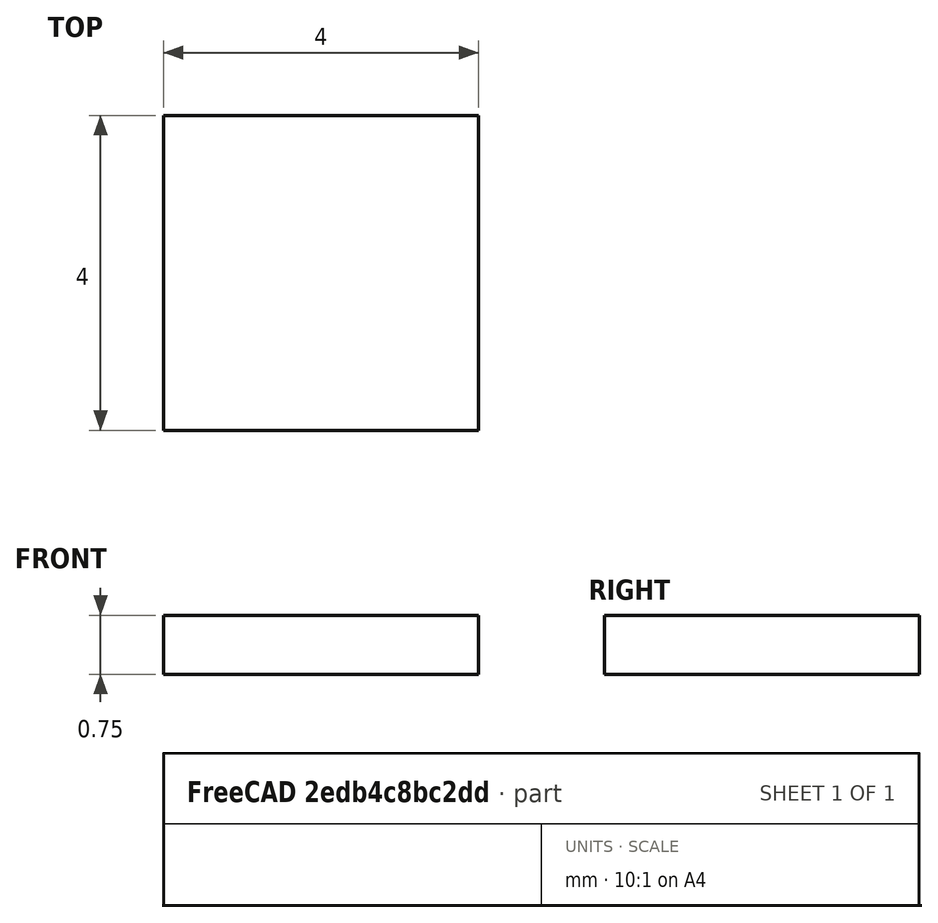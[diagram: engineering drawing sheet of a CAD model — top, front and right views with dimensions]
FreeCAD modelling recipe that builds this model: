
FCSTD DOCUMENT  (FreeCAD 0.18R4 (GitTag))
Label: yp2233w
License: All rights reserved
LicenseURL: http://en.wikipedia.org/wiki/All_rights_reserved
objects: Sketcher::SketchObject×1, PartDesign::Pad×1, PartDesign::Body×1
note: 4 computed .brp shape members not serialized (recipe doc carries the construction recipe); baked Part::Feature solids carry a one-line shape summary decoded from their .brp

FEATURE [Sketcher::SketchObject] Sketch
  MapMode = 5
  Support = -> [XY_Plane]
  sketch-geometry (4):
    g0: LineSegment StartX=-2 StartY=2 StartZ=0 EndX=2 EndY=2 EndZ=0
    g1: LineSegment StartX=2 StartY=2 StartZ=0 EndX=2 EndY=-2 EndZ=0
    g2: LineSegment StartX=2 StartY=-2 StartZ=0 EndX=-2 EndY=-2 EndZ=0
    g3: LineSegment StartX=-2 StartY=-2 StartZ=0 EndX=-2 EndY=2 EndZ=0
  constraints (12):
    c: Coincident(g0,g1)
    c: Coincident(g1,g2)
    c: Coincident(g2,g3)
    c: Coincident(g3,g0)
    c: Horizontal(g0)
    c: Horizontal(g2)
    c: Vertical(g1)
    c: Vertical(g3)
    c: DistanceX(g-1,g0) = 2
    c: DistanceX(g0,g0) = 4
    c: DistanceY(g-1,g0) = 2
    c: DistanceY(g1,g0) = 4
FEATURE [PartDesign::Pad] Pad
  Length = 0.75
  Length2 = 100
  Profile = -> Sketch
  Type = 0
FEATURE [PartDesign::Body] Body
  Group = -> [Sketch,Pad]
  Origin = -> Origin
  Tip = -> Pad
